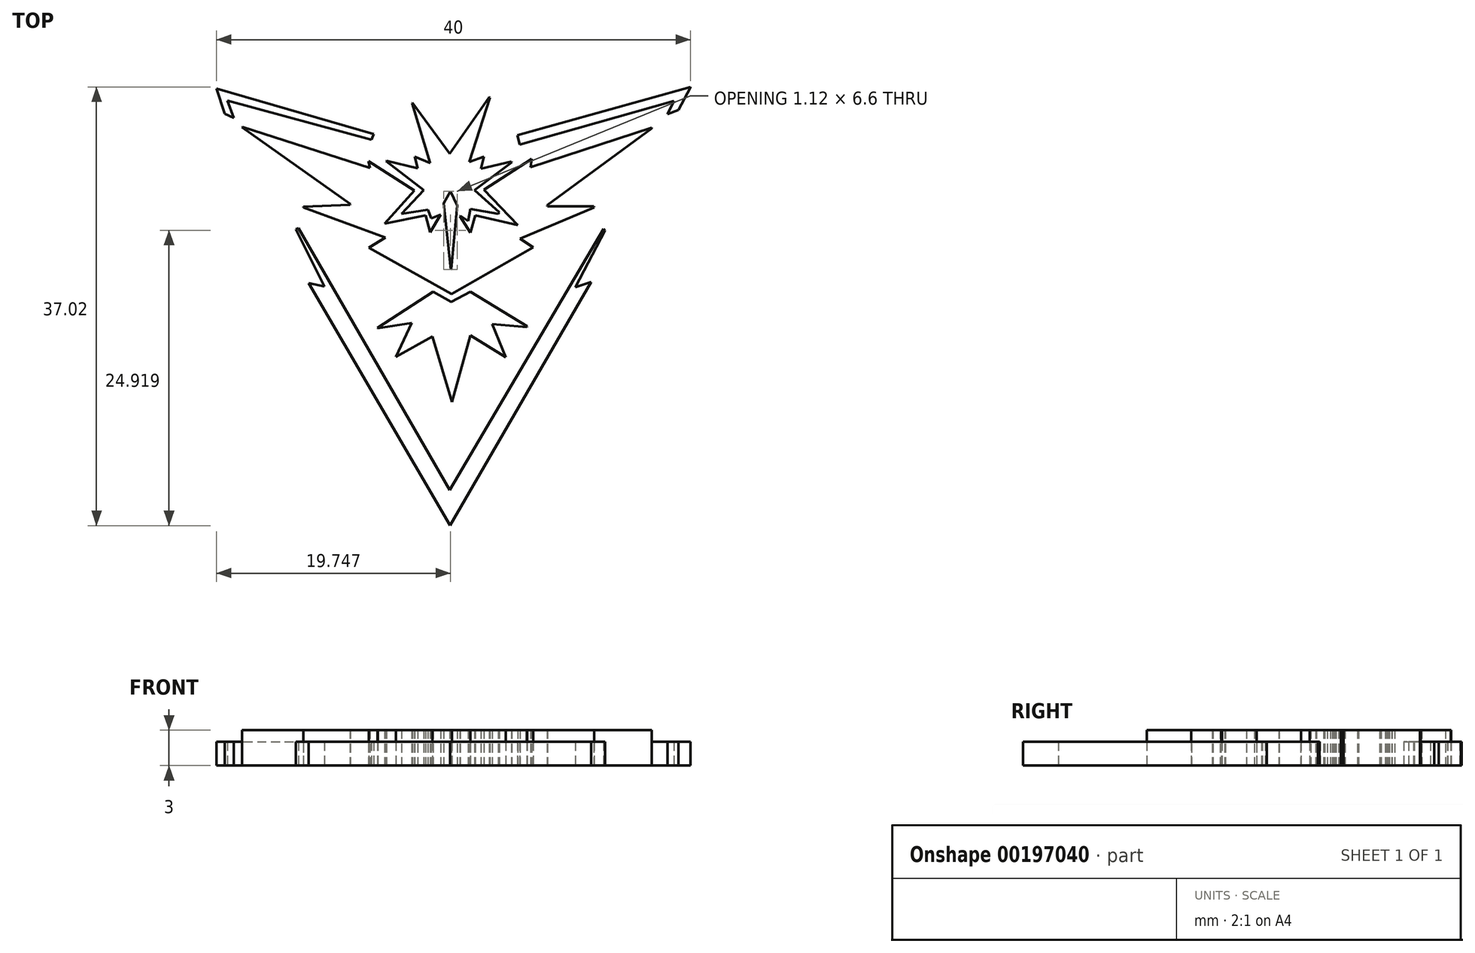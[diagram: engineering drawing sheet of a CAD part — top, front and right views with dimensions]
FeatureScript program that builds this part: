
annotation { "Feature Type Name" : "Feature", "Feature Type Description" : "" }
export const myFeature = defineFeature(function(context is Context, id is Id, definition is map)
    precondition{}
    {
        {
            var Q0;
            Q0=qCreatedBy(makeId("Top.planeOp"),FACE);
            var sketch = newSketch(context, id + "F0", { "sketchPlane" : qUnion([Q0])});
            skLineSegment(sketch, "E0", {"start": v(20, 18.47) * mm, "end": v(19, 16.57) * mm});
            skLineSegment(sketch, "E1", {"start": v(19, 16.57) * mm, "end": v(18.07, 16.21) * mm});
            skLineSegment(sketch, "E2", {"start": v(18.07, 16.21) * mm, "end": v(18.62, 17.32) * mm});
            skLineSegment(sketch, "E3", {"start": v(18.62, 17.32) * mm, "end": v(5.58, 13.63) * mm});
            skLineSegment(sketch, "E4", {"start": v(5.58, 13.63) * mm, "end": v(5.41, 14.45) * mm});
            skLineSegment(sketch, "E5", {"start": v(5.41, 14.45) * mm, "end": v(20, 18.5) * mm});
            skLineSegment(sketch, "E6", {"start": v(20, 18.5) * mm, "end": v(20, 18.47) * mm});
            skLineSegment(sketch, "E7", {"start": v(16.74, 15.01) * mm, "end": v(7.9, 8.54) * mm});
            skLineSegment(sketch, "E8", {"start": v(7.9, 8.54) * mm, "end": v(7.92, 8.44) * mm});
            skLineSegment(sketch, "E9", {"start": v(7.92, 8.44) * mm, "end": v(11.86, 8.44) * mm});
            skLineSegment(sketch, "E10", {"start": v(11.86, 8.44) * mm, "end": v(11.87, 8.34) * mm});
            skLineSegment(sketch, "E11", {"start": v(11.87, 8.34) * mm, "end": v(5.61, 5.7) * mm});
            skLineSegment(sketch, "E12", {"start": v(5.61, 5.7) * mm, "end": v(6.72, 4.98) * mm});
            skLineSegment(sketch, "E13", {"start": v(6.72, 4.98) * mm, "end": v(-0.17, 1.04) * mm});
            skLineSegment(sketch, "E14", {"start": v(-0.17, 1.04) * mm, "end": v(-7.13, 4.93) * mm});
            skLineSegment(sketch, "E15", {"start": v(-7.13, 4.93) * mm, "end": v(-5.75, 5.78) * mm});
            skLineSegment(sketch, "E16", {"start": v(-5.75, 5.78) * mm, "end": v(-12.68, 8.34) * mm});
            skLineSegment(sketch, "E17", {"start": v(-12.68, 8.34) * mm, "end": v(-12.67, 8.4) * mm});
            skLineSegment(sketch, "E18", {"start": v(-12.67, 8.4) * mm, "end": v(-8.72, 8.55) * mm});
            skLineSegment(sketch, "E19", {"start": v(-8.72, 8.55) * mm, "end": v(-8.68, 8.62) * mm});
            skLineSegment(sketch, "E20", {"start": v(-8.68, 8.62) * mm, "end": v(-17.83, 15.1) * mm});
            skLineSegment(sketch, "E21", {"start": v(-17.83, 15.1) * mm, "end": v(-17.81, 15.15) * mm});
            skLineSegment(sketch, "E22", {"start": v(-17.81, 15.15) * mm, "end": v(-7.04, 11.66) * mm});
            skLineSegment(sketch, "E23", {"start": v(-7.04, 11.66) * mm, "end": v(-7.16, 12.24) * mm});
            skLineSegment(sketch, "E24", {"start": v(-7.16, 12.24) * mm, "end": v(-3.3, 9.76) * mm});
            skLineSegment(sketch, "E25", {"start": v(-3.3, 9.76) * mm, "end": v(-5.82, 6.98) * mm});
            skLineSegment(sketch, "E26", {"start": v(-5.82, 6.98) * mm, "end": v(-2.36, 7.67) * mm});
            skLineSegment(sketch, "E27", {"start": v(-2.36, 7.67) * mm, "end": v(-1.97, 6.25) * mm});
            skLineSegment(sketch, "E28", {"start": v(-1.97, 6.25) * mm, "end": v(-1.07, 7.73) * mm});
            skLineSegment(sketch, "E29", {"start": v(-1.07, 7.73) * mm, "end": v(-1.87, 7.43) * mm});
            skLineSegment(sketch, "E30", {"start": v(-1.87, 7.43) * mm, "end": v(-2.15, 8.14) * mm});
            skLineSegment(sketch, "E31", {"start": v(-2.15, 8.14) * mm, "end": v(-4.39, 7.8) * mm});
            skLineSegment(sketch, "E32", {"start": v(-4.39, 7.8) * mm, "end": v(-2.5, 9.8) * mm});
            skLineSegment(sketch, "E33", {"start": v(-2.5, 9.8) * mm, "end": v(-5.7, 12.24) * mm});
            skLineSegment(sketch, "E34", {"start": v(-5.7, 12.24) * mm, "end": v(-5.66, 12.29) * mm});
            skLineSegment(sketch, "E35", {"start": v(-5.66, 12.29) * mm, "end": v(-3.02, 11.63) * mm});
            skLineSegment(sketch, "E36", {"start": v(-3.02, 11.63) * mm, "end": v(-3.27, 12.64) * mm});
            skLineSegment(sketch, "E37", {"start": v(-3.27, 12.64) * mm, "end": v(-1.96, 12.08) * mm});
            skLineSegment(sketch, "E38", {"start": v(-1.96, 12.08) * mm, "end": v(-3.5, 17.14) * mm});
            skLineSegment(sketch, "E39", {"start": v(-3.5, 17.14) * mm, "end": v(-3.45, 17.17) * mm});
            skLineSegment(sketch, "E40", {"start": v(-3.45, 17.17) * mm, "end": v(-0.32, 12.88) * mm});
            skLineSegment(sketch, "E41", {"start": v(-0.32, 12.88) * mm, "end": v(3.03, 17.63) * mm});
            skLineSegment(sketch, "E42", {"start": v(3.03, 17.63) * mm, "end": v(3.07, 17.61) * mm});
            skLineSegment(sketch, "E43", {"start": v(3.07, 17.61) * mm, "end": v(1.33, 12.17) * mm});
            skLineSegment(sketch, "E44", {"start": v(1.33, 12.17) * mm, "end": v(2.57, 12.63) * mm});
            skLineSegment(sketch, "E45", {"start": v(2.57, 12.63) * mm, "end": v(2.33, 11.6) * mm});
            skLineSegment(sketch, "E46", {"start": v(2.33, 11.6) * mm, "end": v(4.89, 12.21) * mm});
            skLineSegment(sketch, "E47", {"start": v(4.89, 12.21) * mm, "end": v(4.92, 12.15) * mm});
            skLineSegment(sketch, "E48", {"start": v(4.92, 12.15) * mm, "end": v(1.8, 9.8) * mm});
            skLineSegment(sketch, "E49", {"start": v(1.8, 9.8) * mm, "end": v(3.89, 7.92) * mm});
            skLineSegment(sketch, "E50", {"start": v(3.89, 7.92) * mm, "end": v(3.8, 7.78) * mm});
            skLineSegment(sketch, "E51", {"start": v(3.8, 7.78) * mm, "end": v(1.43, 8.22) * mm});
            skLineSegment(sketch, "E52", {"start": v(1.43, 8.22) * mm, "end": v(1.24, 7.18) * mm});
            skLineSegment(sketch, "E53", {"start": v(1.24, 7.18) * mm, "end": v(0.59, 7.65) * mm});
            skLineSegment(sketch, "E54", {"start": v(0.59, 7.65) * mm, "end": v(0.55, 7.61) * mm});
            skLineSegment(sketch, "E55", {"start": v(0.55, 7.61) * mm, "end": v(1.43, 6.2) * mm});
            skLineSegment(sketch, "E56", {"start": v(1.43, 6.2) * mm, "end": v(1.84, 7.67) * mm});
            skLineSegment(sketch, "E57", {"start": v(1.84, 7.67) * mm, "end": v(5.44, 6.86) * mm});
            skLineSegment(sketch, "E58", {"start": v(5.44, 6.86) * mm, "end": v(2.57, 9.84) * mm});
            skLineSegment(sketch, "E59", {"start": v(2.57, 9.84) * mm, "end": v(6.61, 12.43) * mm});
            skLineSegment(sketch, "E60", {"start": v(6.61, 12.43) * mm, "end": v(6.5, 11.73) * mm});
            skLineSegment(sketch, "E61", {"start": v(6.5, 11.73) * mm, "end": v(16.72, 15.06) * mm});
            skLineSegment(sketch, "E62", {"start": v(16.72, 15.06) * mm, "end": v(16.74, 15.01) * mm});
            skLineSegment(sketch, "E63", {"start": v(-0.23, 3.1) * mm, "end": v(-0.19, 3.12) * mm});
            skLineSegment(sketch, "E64", {"start": v(-0.19, 3.12) * mm, "end": v(0.3, 8.48) * mm});
            skLineSegment(sketch, "E65", {"start": v(0.3, 8.48) * mm, "end": v(-0.24, 9.71) * mm});
            skLineSegment(sketch, "E66", {"start": v(-0.24, 9.71) * mm, "end": v(-0.81, 8.67) * mm});
            skLineSegment(sketch, "E67", {"start": v(-0.81, 8.67) * mm, "end": v(-0.23, 3.1) * mm});
            skLineSegment(sketch, "E68", {"start": v(12.78, 6.4) * mm, "end": v(10.27, 1.62) * mm});
            skLineSegment(sketch, "E69", {"start": v(10.27, 1.62) * mm, "end": v(11.62, 2.06) * mm});
            skLineSegment(sketch, "E70", {"start": v(11.62, 2.06) * mm, "end": v(-0.27, -18.5) * mm});
            skLineSegment(sketch, "E71", {"start": v(-0.27, -18.5) * mm, "end": v(-12.22, 1.94) * mm});
            skLineSegment(sketch, "E72", {"start": v(-12.22, 1.94) * mm, "end": v(-10.9, 1.68) * mm});
            skLineSegment(sketch, "E73", {"start": v(-10.9, 1.68) * mm, "end": v(-13.3, 6.48) * mm});
            skLineSegment(sketch, "E74", {"start": v(-13.3, 6.48) * mm, "end": v(-13.07, 6.59) * mm});
            skLineSegment(sketch, "E75", {"start": v(-13.07, 6.59) * mm, "end": v(-0.32, -15.5) * mm});
            skLineSegment(sketch, "E76", {"start": v(-0.32, -15.5) * mm, "end": v(12.68, 6.51) * mm});
            skLineSegment(sketch, "E77", {"start": v(12.68, 6.51) * mm, "end": v(12.78, 6.4) * mm});
            skLineSegment(sketch, "E78", {"start": v(-1.77, -2.54) * mm, "end": v(-4.86, -4.28) * mm});
            skLineSegment(sketch, "E79", {"start": v(-4.86, -4.28) * mm, "end": v(-3.53, -1.42) * mm});
            skLineSegment(sketch, "E80", {"start": v(-3.53, -1.42) * mm, "end": v(-6.4, -1.86) * mm});
            skLineSegment(sketch, "E81", {"start": v(-6.4, -1.86) * mm, "end": v(-6.42, -1.8) * mm});
            skLineSegment(sketch, "E82", {"start": v(-6.42, -1.8) * mm, "end": v(-1.71, 1.23) * mm});
            skLineSegment(sketch, "E83", {"start": v(-1.71, 1.23) * mm, "end": v(-0.18, 0.36) * mm});
            skLineSegment(sketch, "E84", {"start": v(-0.18, 0.36) * mm, "end": v(1.43, 1.23) * mm});
            skLineSegment(sketch, "E85", {"start": v(1.43, 1.23) * mm, "end": v(6.22, -1.7) * mm});
            skLineSegment(sketch, "E86", {"start": v(6.22, -1.7) * mm, "end": v(6.2, -1.76) * mm});
            skLineSegment(sketch, "E87", {"start": v(6.2, -1.76) * mm, "end": v(3.26, -1.5) * mm});
            skLineSegment(sketch, "E88", {"start": v(3.26, -1.5) * mm, "end": v(4.42, -4.31) * mm});
            skLineSegment(sketch, "E89", {"start": v(4.42, -4.31) * mm, "end": v(1.42, -2.46) * mm});
            skLineSegment(sketch, "E90", {"start": v(1.42, -2.46) * mm, "end": v(-0.13, -8.06) * mm});
            skLineSegment(sketch, "E91", {"start": v(-0.13, -8.06) * mm, "end": v(-1.77, -2.54) * mm});
            skLineSegment(sketch, "E92", {"start": v(-6.74, 14.52) * mm, "end": v(-6.93, 14.05) * mm});
            skLineSegment(sketch, "E93", {"start": v(-6.93, 14.05) * mm, "end": v(-19.09, 17.34) * mm});
            skLineSegment(sketch, "E94", {"start": v(-19.09, 17.34) * mm, "end": v(-18.55, 15.88) * mm});
            skLineSegment(sketch, "E95", {"start": v(-18.55, 15.88) * mm, "end": v(-19.3, 16.23) * mm});
            skLineSegment(sketch, "E96", {"start": v(-19.3, 16.23) * mm, "end": v(-20, 18.38) * mm});
            skLineSegment(sketch, "E97", {"start": v(-20, 18.38) * mm, "end": v(-6.74, 14.52) * mm});
            skSolve(sketch);
        }
        {
            var Q0;
            Q0=makeQuery(id+"F0.imprint","IMPRINT",FACE,{"disambiguationData":[TD([[makeQuery(id+"F0.imprint","IMPRINT",EDGE,{"derivedFrom":sQuery(id+"F0.wireOp",EDGE,"E7")}),-1.0]])]});
            var Q1;
            Q1=makeQuery(id+"F0.imprint","IMPRINT",FACE,{"disambiguationData":[TD([[makeQuery(id+"F0.imprint","IMPRINT",EDGE,{"derivedFrom":sQuery(id+"F0.wireOp",EDGE,"E78")}),-1.0]])]});
            extrude(context, id + "F1", {"entities" : qUnion([Q0, Q1]), "depth" : 3 * mm});
        }
        {
            var Q0;
            Q0=makeQuery(id+"F0.imprint","IMPRINT",FACE,{"disambiguationData":[TD([[makeQuery(id+"F0.imprint","IMPRINT",EDGE,{"derivedFrom":sQuery(id+"F0.wireOp",EDGE,"E92")}),-1.0]])]});
            var Q1;
            Q1=makeQuery(id+"F0.imprint","IMPRINT",FACE,{"disambiguationData":[TD([[makeQuery(id+"F0.imprint","IMPRINT",EDGE,{"derivedFrom":sQuery(id+"F0.wireOp",EDGE,"E0")}),-1.0]])]});
            var Q2;
            Q2=makeQuery(id+"F0.imprint","IMPRINT",FACE,{"disambiguationData":[TD([[makeQuery(id+"F0.imprint","IMPRINT",EDGE,{"derivedFrom":sQuery(id+"F0.wireOp",EDGE,"E68")}),-1.0]])]});
            extrude(context, id + "F2", {"entities" : qUnion([Q0, Q1, Q2]), "depth" : 2 * mm});
        }
    });
